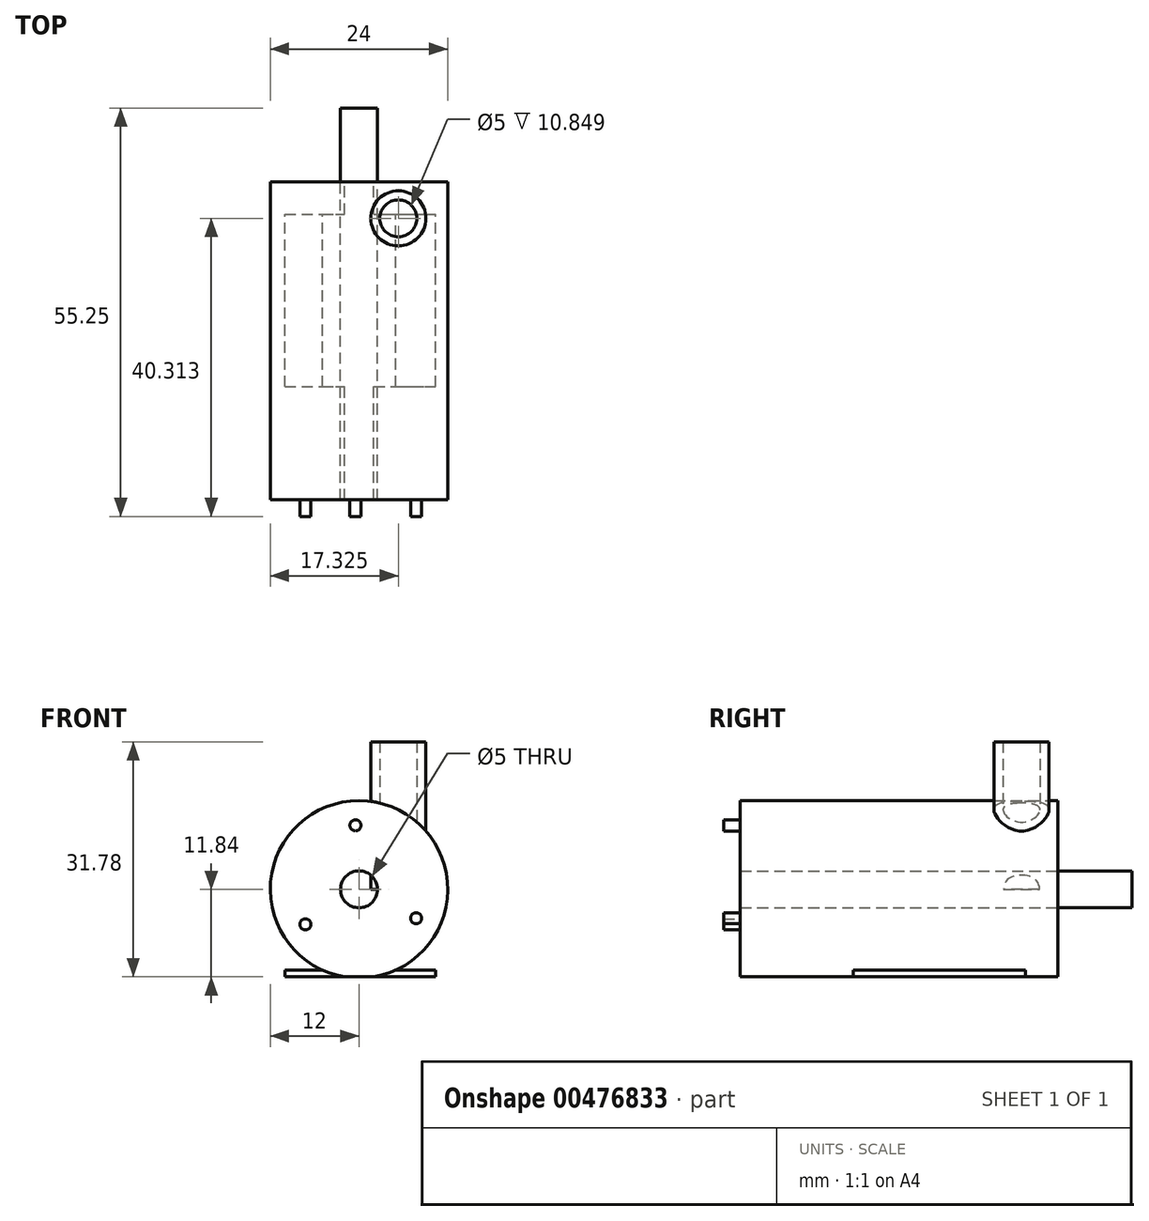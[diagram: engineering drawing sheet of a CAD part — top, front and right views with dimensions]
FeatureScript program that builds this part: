
annotation { "Feature Type Name" : "Feature", "Feature Type Description" : "" }
export const myFeature = defineFeature(function(context is Context, id is Id, definition is map)
    precondition{}
    {
        {
            var Q0;
            Q0=qCreatedBy(makeId("Front.planeOp"),FACE);
            var sketch = newSketch(context, id + "F0", { "sketchPlane" : qUnion([Q0])});
            skLineSegment(sketch, "E0", {"start": v(-99.76, 30.95) * mm, "end": v(0, 0) * mm, "construction": true});
            skLineSegment(sketch, "E1", {"start": v(0, 0) * mm, "end": v(31.2, 30.95) * mm, "construction": true});
            skLineSegment(sketch, "E2", {"start": v(-99.76, -98.27) * mm, "end": v(-28.68, -12.78) * mm, "construction": true});
            skLineSegment(sketch, "E3", {"start": v(-28.68, -12.78) * mm, "end": v(31.2, -98.27) * mm, "construction": true});
            skLineSegment(sketch, "E4", {"start": v(-71.28, -13.22) * mm, "end": v(-99.76, -98.27) * mm, "construction": true});
            skLineSegment(sketch, "E5", {"start": v(-71.28, -13.22) * mm, "end": v(-99.76, 30.95) * mm, "construction": true});
            skPoint(sketch, "E6", {"position": v(-66.94, -13.24) * mm});
            skPoint(sketch, "E7", {"position": v(-43.6, -13.24) * mm});
            skPoint(sketch, "E8", {"position": v(-36.94, 10.23) * mm});
            skLineSegment(sketch, "E9", {"start": v(1.6, 19.94) * mm, "end": v(9.05, 19.94) * mm, "construction": true});
            skPoint(sketch, "E10", {"position": v(-28.63, 8.5) * mm});
            skPoint(sketch, "E11", {"position": v(-26.34, 8.5) * mm});
            skSolve(sketch);
        }
        {
            var Q0;
            Q0=qCreatedBy(makeId("Front.planeOp"),FACE);
            var sketch = newSketch(context, id + "F1", { "sketchPlane" : qUnion([Q0])});
            skCircle(sketch, "E12", {"center": v(0, 0) * mm, "radius": 2.5 * mm});
            skCircle(sketch, "E13", {"center": v(0, 0) * mm, "radius": 12 * mm});
            skLineSegment(sketch, "E14.bottom", {"start": v(-10.05, -10.92) * mm, "end": v(10.36, -10.92) * mm});
            skLineSegment(sketch, "E14.top", {"start": v(-10.05, -11.84) * mm, "end": v(10.36, -11.84) * mm});
            skLineSegment(sketch, "E14.left", {"start": v(-10.05, -10.92) * mm, "end": v(-10.05, -11.84) * mm});
            skLineSegment(sketch, "E14.right", {"start": v(10.36, -10.92) * mm, "end": v(10.36, -11.84) * mm});
            skSolve(sketch);
        }
        {
            var Q0;
            Q0=makeQuery(id+"F1.imprint","IMPRINT",FACE,{"disambiguationData":[TD([[makeQuery(id+"F1.imprint","IMPRINT",EDGE,{"derivedFrom":sQuery(id+"F1.wireOp",EDGE,"E12")}),-1.0]])]});
            var Q1;
            {var subQ0=sQuery(id+"F1.wireOp",EDGE,"E14.top");var subQ1=sQuery(id+"F1.wireOp",EDGE,"E13");var subQ2=makeQuery(id+"F1.imprint","INTERSECT",VERTEX,{"disambiguationData":[OD(0.0)],"derivedFrom":[subQ1,subQ0]});Q1=makeQuery(id+"F1.imprint","IMPRINT",FACE,{"disambiguationData":[TD([[makeQuery(id+"F1.imprint","IMPRINT",EDGE,{"disambiguationData":[TD([[subQ2,1.0]])],"derivedFrom":subQ1}),1.0]])]});}
            extrude(context, id + "F2", {"entities" : qUnion([Q0, Q1]), "depth" : 43 * mm});
        }
        {
            var Q0;
            {var subQ5=sQuery(id+"F1.wireOp",EDGE,"E14.left");Q0=makeQuery(id+"F1.imprint","IMPRINT",FACE,{"disambiguationData":[TD([[makeQuery(id+"F1.imprint","IMPRINT",EDGE,{"derivedFrom":subQ5}),1.0]])]});}
            var Q1;
            {var subQ5=sQuery(id+"F1.wireOp",EDGE,"E14.right");Q1=makeQuery(id+"F1.imprint","IMPRINT",FACE,{"disambiguationData":[TD([[makeQuery(id+"F1.imprint","IMPRINT",EDGE,{"derivedFrom":subQ5}),-1.0]])]});}
            var Q2;
            {var subQ0=sQuery(id+"F1.wireOp",EDGE,"E14.top");var subQ1=sQuery(id+"F1.wireOp",EDGE,"E13");var subQ2=makeQuery(id+"F1.imprint","INTERSECT",VERTEX,{"disambiguationData":[OD(0.0)],"derivedFrom":[subQ1,subQ0]});Q2=makeQuery(id+"F1.imprint","IMPRINT",FACE,{"disambiguationData":[TD([[makeQuery(id+"F1.imprint","IMPRINT",EDGE,{"disambiguationData":[TD([[subQ2,1.0]])],"derivedFrom":subQ1}),1.0]])]});}
            extrude(context, id + "F3", {"entities" : qUnion([Q0, Q1, Q2]), "operationType" : NewBodyOperationType.ADD, "depth" : 27.7 * mm, "hasSecondDirection" : true, "secondDirectionOppositeDirection" : false, "secondDirectionDepth" : 4.4 * mm});
        }
        {
            var Q0;
            Q0=qCreatedBy(makeId("Top.planeOp"),FACE);
            var sketch = newSketch(context, id + "F4", { "sketchPlane" : qUnion([Q0])});
            skCircle(sketch, "E15", {"center": v(5.32, -4.94) * mm, "radius": 3.73 * mm});
            skPoint(sketch, "E16.0", {"position": v(1.6, 0) * mm});
            skPoint(sketch, "E17.0", {"position": v(9.05, 0) * mm});
            skLineSegment(sketch, "E18", {"start": v(1.6, 0) * mm, "end": v(1.6, -4.94) * mm, "construction": true});
            skLineSegment(sketch, "E19", {"start": v(9.05, 0) * mm, "end": v(9.05, -4.94) * mm, "construction": true});
            skCircle(sketch, "E20", {"center": v(5.32, -4.94) * mm, "radius": 2.5 * mm});
            skSolve(sketch);
        }
        {
            var Q0;
            Q0=qSketchRegion(id+"F4",true);
            var Q1;
            Q1=sQuery(id+"F0.wireOp",VERTEX,"E9.end");
            extrude(context, id + "F5", {"entities" : qUnion([Q0]), "operationType" : NewBodyOperationType.ADD, "endBound" : BoundingType.UP_TO_VERTEX, "endBoundEntityVertex" : qUnion([Q1]), "depth" : 25 * mm});
        }
        {
            var Q0;
            Q0=makeQuery(id+"F2.opExtrude","CAP_FACE",FACE,{"disambiguationData":[OSD([sQuery(id+"F1.wireOp",EDGE,"E12"),sQuery(id+"F1.wireOp",EDGE,"E13"),sQuery(id+"F1.wireOp",EDGE,"E14.top")])],"isStart":false});
            var sketch = newSketch(context, id + "F6", { "sketchPlane" : qUnion([Q0])});
            skCircle(sketch, "E21", {"center": v(-0.48, 8.65) * mm, "radius": 0.75 * mm});
            skLineSegment(sketch, "E22", {"start": v(-0.48, 8.65) * mm, "end": v(0, 0) * mm, "construction": true});
            skCircle(sketch, "E23.1.0", {"center": v(-7.25, -4.74) * mm, "radius": 0.75 * mm});
            skCircle(sketch, "E23.2.0", {"center": v(7.73, -3.9) * mm, "radius": 0.75 * mm});
            skPoint(sketch, "E23.center", {"position": v(0, 0) * mm});
            skSolve(sketch);
        }
        {
            var Q0;
            Q0=qSketchRegion(id+"F6",true);
            extrude(context, id + "F7", {"entities" : qUnion([Q0]), "operationType" : NewBodyOperationType.ADD, "depth" : 2.25 * mm});
        }
        {
            var Q0;
            Q0=makeQuery(id+"F1.imprint","IMPRINT",FACE,{"disambiguationData":[TD([[makeQuery(id+"F1.imprint","IMPRINT",EDGE,{"derivedFrom":sQuery(id+"F1.wireOp",EDGE,"E12")}),1.0]])]});
            extrude(context, id + "F8", {"entities" : qUnion([Q0]), "oppositeDirection" : true, "depth" : 10 * mm});
        }
    });
